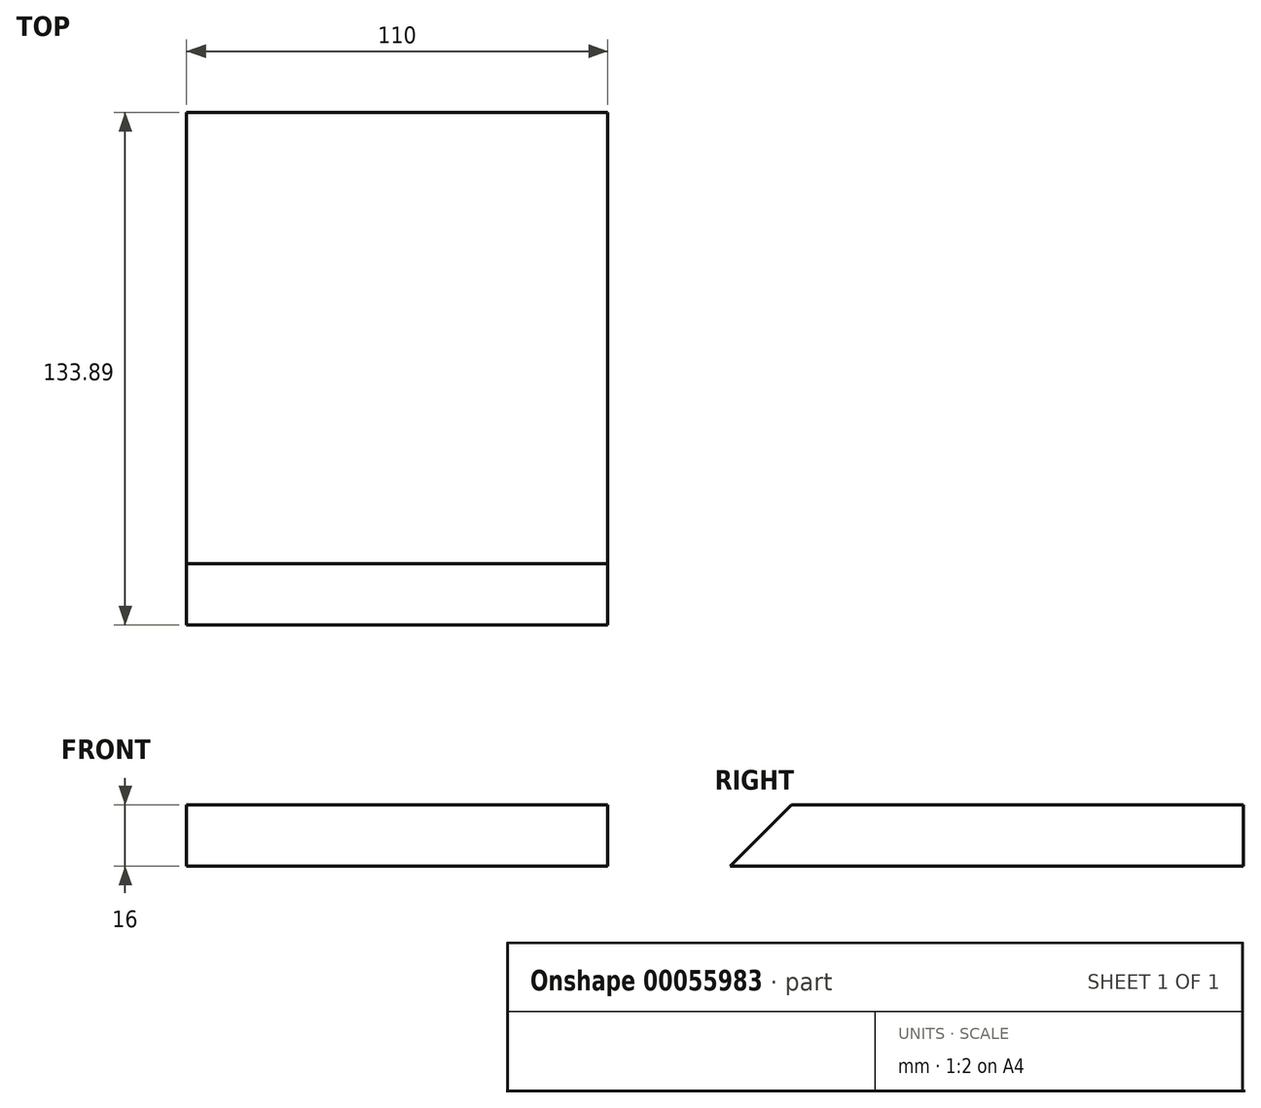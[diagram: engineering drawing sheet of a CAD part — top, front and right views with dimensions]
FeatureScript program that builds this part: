
annotation { "Feature Type Name" : "Feature", "Feature Type Description" : "" }
export const myFeature = defineFeature(function(context is Context, id is Id, definition is map)
    precondition{}
    {
        {
            var Q0;
            Q0=qCreatedBy(makeId("Top.planeOp"),FACE);
            var sketch = newSketch(context, id + "F0", { "sketchPlane" : qUnion([Q0])});
            skLineSegment(sketch, "E0.bottom", {"start": v(0, 0) * mm, "end": v(110, 0) * mm});
            skLineSegment(sketch, "E0.top", {"start": v(0, 133.89) * mm, "end": v(110, 133.89) * mm});
            skLineSegment(sketch, "E0.left", {"start": v(0, 0) * mm, "end": v(0, 133.89) * mm});
            skLineSegment(sketch, "E0.right", {"start": v(110, 0) * mm, "end": v(110, 133.89) * mm});
            skSolve(sketch);
        }
        {
            var Q0;
            Q0=makeQuery(id+"F0.imprint","IMPRINT",FACE,{"disambiguationData":[TD([[makeQuery(id+"F0.imprint","IMPRINT",EDGE,{"derivedFrom":sQuery(id+"F0.wireOp",EDGE,"E0.bottom")}),1.0]])]});
            extrude(context, id + "F1", {"entities" : qUnion([Q0]), "depth" : 16 * mm});
        }
        {
            var Q0;
            Q0=makeQuery(id+"F1.opExtrude","CAP_EDGE",EDGE,{"disambiguationData":[OSD([sQuery(id+"F0.wireOp",EDGE,"E0.bottom")])],"isStart":false});
            chamfer(context, id + "F2", {"entities" : qUnion([Q0]), "width" : 16 * mm, "tangentPropagation" : true});
        }
    });
